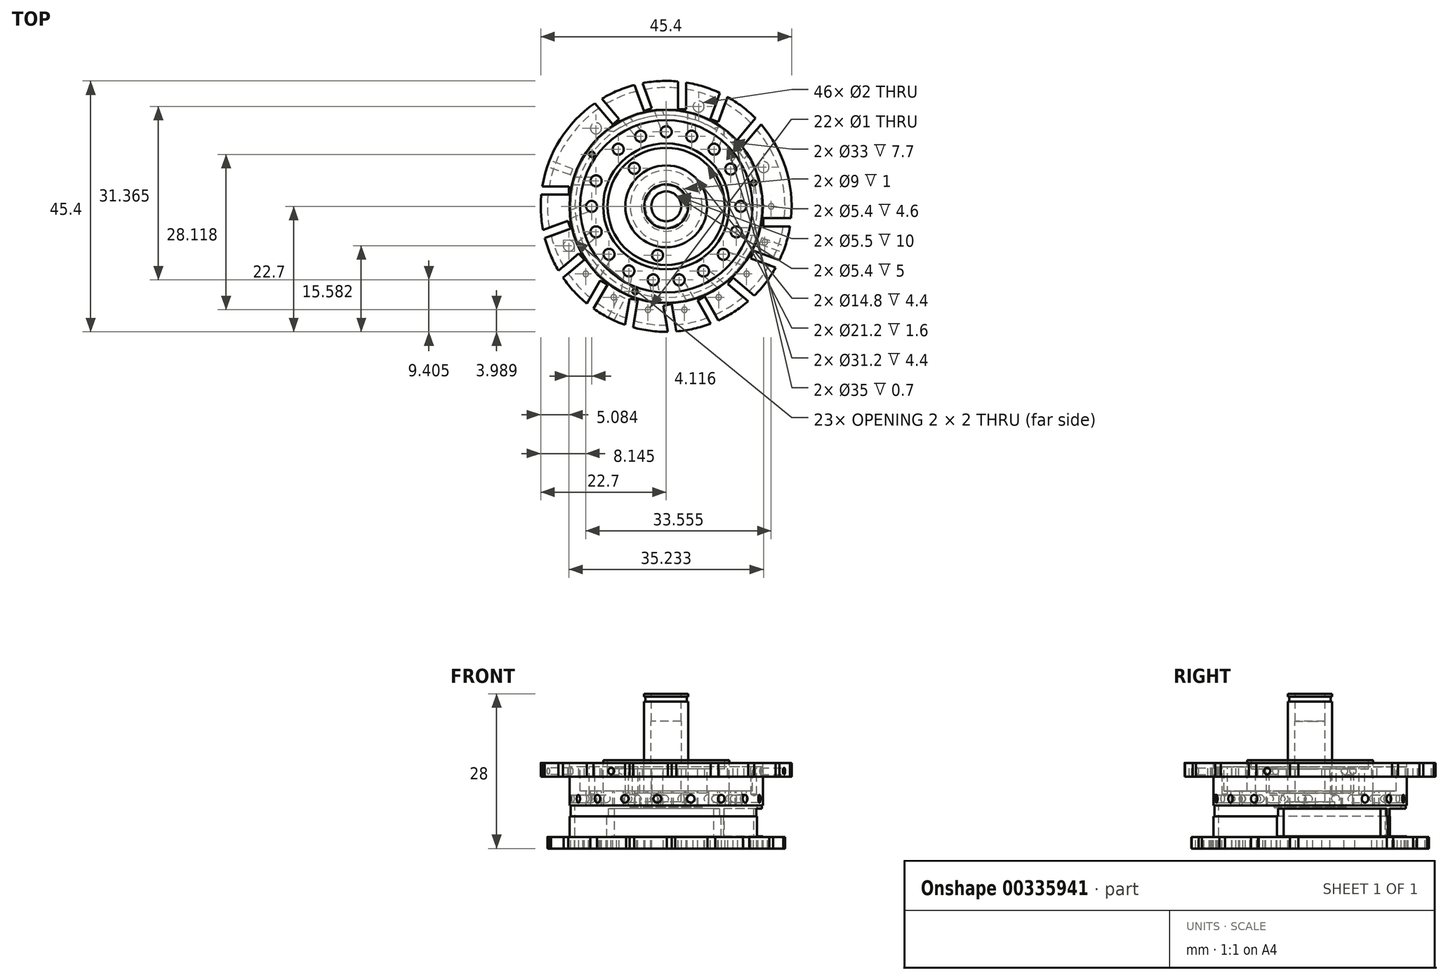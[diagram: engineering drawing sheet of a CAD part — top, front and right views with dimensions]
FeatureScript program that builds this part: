
annotation { "Feature Type Name" : "Feature", "Feature Type Description" : "" }
export const myFeature = defineFeature(function(context is Context, id is Id, definition is map)
    precondition{}
    {
        {
            var Q0;
            Q0=qCreatedBy(makeId("Front.planeOp"),FACE);
            var sketch = newSketch(context, id + "F0", { "sketchPlane" : qUnion([Q0])});
            skLineSegment(sketch, "E0", {"start": v(-16.5, 0) * mm, "end": v(-16.5, 7.7) * mm});
            skLineSegment(sketch, "E1", {"start": v(-16.5, 7.7) * mm, "end": v(-6.5, 7.7) * mm});
            skLineSegment(sketch, "E2", {"start": v(-6.5, 7.7) * mm, "end": v(-6.5, 7.4) * mm});
            skLineSegment(sketch, "E3", {"start": v(-6.5, 7.4) * mm, "end": v(-4.5, 7.4) * mm});
            skLineSegment(sketch, "E4", {"start": v(-4.5, 7.4) * mm, "end": v(-4.5, 8.4) * mm});
            skLineSegment(sketch, "E5", {"start": v(-4.5, 8.4) * mm, "end": v(-2.7, 8.4) * mm});
            skLineSegment(sketch, "E6", {"start": v(-2.7, 8.4) * mm, "end": v(-2.7, 13) * mm});
            skLineSegment(sketch, "E7", {"start": v(-2.7, 13) * mm, "end": v(-2.75, 13) * mm});
            skLineSegment(sketch, "E8", {"start": v(-2.75, 13) * mm, "end": v(-2.75, 23) * mm});
            skLineSegment(sketch, "E9", {"start": v(-2.75, 23) * mm, "end": v(-2.7, 23) * mm});
            skLineSegment(sketch, "E10", {"start": v(-2.7, 23) * mm, "end": v(-2.7, 28) * mm});
            skLineSegment(sketch, "E11", {"start": v(-2.7, 28) * mm, "end": v(-4, 28) * mm});
            skLineSegment(sketch, "E12", {"start": v(-4, 28) * mm, "end": v(-4, 27.5) * mm});
            skLineSegment(sketch, "E13", {"start": v(-4, 27.5) * mm, "end": v(-3.75, 27.5) * mm});
            skLineSegment(sketch, "E14", {"start": v(-3.75, 27.5) * mm, "end": v(-3.75, 26.6) * mm});
            skLineSegment(sketch, "E15", {"start": v(-3.75, 26.6) * mm, "end": v(-4, 26.6) * mm});
            skLineSegment(sketch, "E16", {"start": v(-4, 26.6) * mm, "end": v(-4, 10) * mm});
            skLineSegment(sketch, "E17", {"start": v(-4, 10) * mm, "end": v(-7.4, 10) * mm});
            skLineSegment(sketch, "E18", {"start": v(-7.4, 10) * mm, "end": v(-7.4, 14.4) * mm});
            skLineSegment(sketch, "E19", {"start": v(-7.4, 14.4) * mm, "end": v(-10.6, 14.4) * mm});
            skLineSegment(sketch, "E20", {"start": v(-10.6, 14.4) * mm, "end": v(-10.6, 16) * mm});
            skLineSegment(sketch, "E21", {"start": v(-10.6, 16) * mm, "end": v(-11.4, 16) * mm});
            skLineSegment(sketch, "E22", {"start": v(-11.4, 16) * mm, "end": v(-11.4, 10.4) * mm});
            skLineSegment(sketch, "E23", {"start": v(-22.7, 15.5) * mm, "end": v(-22.7, 13) * mm});
            skLineSegment(sketch, "E24", {"start": v(-22.7, 13) * mm, "end": v(-17.5, 13) * mm});
            skLineSegment(sketch, "E25", {"start": v(-17.5, 13) * mm, "end": v(-17.5, 7.8) * mm});
            skLineSegment(sketch, "E26", {"start": v(-17.5, 7.8) * mm, "end": v(-17.3, 7.8) * mm});
            skLineSegment(sketch, "E27", {"start": v(-17.3, 7.8) * mm, "end": v(-17.3, 5.8) * mm});
            skLineSegment(sketch, "E28", {"start": v(-17.3, 5.8) * mm, "end": v(-17.5, 5.8) * mm});
            skLineSegment(sketch, "E29", {"start": v(-17.5, 5.8) * mm, "end": v(-17.5, 2.1) * mm});
            skLineSegment(sketch, "E30", {"start": v(-17.5, 2.1) * mm, "end": v(-21.5, 2.1) * mm});
            skLineSegment(sketch, "E31", {"start": v(-21.5, 2.1) * mm, "end": v(-21.5, 0) * mm});
            skLineSegment(sketch, "E32", {"start": v(-21.5, 0) * mm, "end": v(-16.5, 0) * mm});
            skLineSegment(sketch, "E33", {"start": v(0, 28) * mm, "end": v(0, 0) * mm});
            skLineSegment(sketch, "E34", {"start": v(-11.4, 10.4) * mm, "end": v(-15.6, 10.4) * mm});
            skLineSegment(sketch, "E35", {"start": v(-15.6, 10.4) * mm, "end": v(-15.6, 14.8) * mm});
            skLineSegment(sketch, "E36", {"start": v(-15.6, 14.8) * mm, "end": v(-17.5, 14.8) * mm});
            skLineSegment(sketch, "E37", {"start": v(-17.5, 14.8) * mm, "end": v(-17.5, 15.5) * mm});
            skLineSegment(sketch, "E38", {"start": v(-17.5, 15.5) * mm, "end": v(-22.7, 15.5) * mm});
            skSolve(sketch);
        }
        {
            var Q0;
            Q0 = qSketchRegion(id + "F0", true);
            var Q1;
            Q1=sQuery(id+"F0.wireOp",EDGE,"E33");
            revolve(context, id + "F1", {"entities" : qUnion([Q0]), "axis" : qUnion([Q1]), "revolveType" : RevolveType.FULL});
        }
        {
            var Q0;
            Q0=makeQuery(id+"F1.opRevolve","SWEPT_FACE",FACE,{"disambiguationData":[OSD([sQuery(id+"F0.wireOp",EDGE,"E38")])]});
            var sketch = newSketch(context, id + "F2", { "sketchPlane" : qUnion([Q0])});
            skCircle(sketch, "E39.0", {"center": v(0, 0) * mm, "radius": 22.7 * mm, "construction": true});
            skCircle(sketch, "E40", {"center": v(0, 0) * mm, "radius": 13.5 * mm, "construction": true});
            skCircle(sketch, "E41", {"center": v(13.5, 0) * mm, "radius": 1 * mm});
            skLineSegment(sketch, "E42", {"start": v(0, 0) * mm, "end": v(-8.68, 10.34) * mm, "construction": true});
            skCircle(sketch, "E43", {"center": v(-8.68, 10.34) * mm, "radius": 1 * mm});
            skLineSegment(sketch, "E44", {"start": v(0, 0) * mm, "end": v(21.33, -7.76) * mm, "construction": true});
            skCircle(sketch, "E45", {"center": v(12.69, -4.62) * mm, "radius": 1 * mm});
            skLineSegment(sketch, "E46", {"start": v(12.69, -4.62) * mm, "end": v(22.23, -4.62) * mm, "construction": true});
            skLineSegment(sketch, "E47", {"start": v(22.6, -3.62) * mm, "end": v(17.6, -3.62) * mm});
            skLineSegment(sketch, "E48", {"start": v(17.6, -3.62) * mm, "end": v(17.6, -2.12) * mm});
            skLineSegment(sketch, "E49", {"start": v(17.6, -2.12) * mm, "end": v(22.6, -2.12) * mm});
            skLineSegment(sketch, "E50.1.0", {"start": v(15.81, -8) * mm, "end": v(20.51, -9.72) * mm});
            skLineSegment(sketch, "E50.1.1", {"start": v(20, -11.13) * mm, "end": v(15.3, -9.42) * mm});
            skLineSegment(sketch, "E50.1.2", {"start": v(15.3, -9.42) * mm, "end": v(15.81, -8) * mm});
            skCircle(sketch, "E50.1.3", {"center": v(10.34, -8.68) * mm, "radius": 1 * mm});
            skLineSegment(sketch, "E50.2.0", {"start": v(12.12, -12.93) * mm, "end": v(15.95, -16.15) * mm});
            skLineSegment(sketch, "E50.2.1", {"start": v(14.99, -17.3) * mm, "end": v(11.16, -14.08) * mm});
            skLineSegment(sketch, "E50.2.2", {"start": v(11.16, -14.08) * mm, "end": v(12.12, -12.93) * mm});
            skCircle(sketch, "E50.2.3", {"center": v(6.75, -11.7) * mm, "radius": 1 * mm});
            skLineSegment(sketch, "E50.3.0", {"start": v(6.97, -16.3) * mm, "end": v(9.47, -20.63) * mm});
            skLineSegment(sketch, "E50.3.1", {"start": v(8.17, -21.38) * mm, "end": v(5.67, -17.05) * mm});
            skLineSegment(sketch, "E50.3.2", {"start": v(5.67, -17.05) * mm, "end": v(6.97, -16.3) * mm});
            skCircle(sketch, "E50.3.3", {"center": v(2.34, -13.3) * mm, "radius": 1 * mm});
            skLineSegment(sketch, "E50.4.0", {"start": v(0.97, -17.7) * mm, "end": v(1.84, -22.63) * mm});
            skLineSegment(sketch, "E50.4.1", {"start": v(0.36, -22.89) * mm, "end": v(-0.5, -17.96) * mm});
            skLineSegment(sketch, "E50.4.2", {"start": v(-0.5, -17.96) * mm, "end": v(0.97, -17.7) * mm});
            skCircle(sketch, "E50.4.3", {"center": v(-2.34, -13.3) * mm, "radius": 1 * mm});
            skLineSegment(sketch, "E50.5.0", {"start": v(-5.14, -16.96) * mm, "end": v(-6, -21.9) * mm});
            skLineSegment(sketch, "E50.5.1", {"start": v(-7.49, -21.63) * mm, "end": v(-6.62, -16.7) * mm});
            skLineSegment(sketch, "E50.5.2", {"start": v(-6.62, -16.7) * mm, "end": v(-5.14, -16.96) * mm});
            skCircle(sketch, "E50.5.3", {"center": v(-6.75, -11.7) * mm, "radius": 1 * mm});
            skLineSegment(sketch, "E50.6.0", {"start": v(-10.63, -14.18) * mm, "end": v(-13.13, -18.51) * mm});
            skLineSegment(sketch, "E50.6.1", {"start": v(-14.43, -17.76) * mm, "end": v(-11.93, -13.43) * mm});
            skLineSegment(sketch, "E50.6.2", {"start": v(-11.93, -13.43) * mm, "end": v(-10.63, -14.18) * mm});
            skCircle(sketch, "E50.6.3", {"center": v(-10.34, -8.68) * mm, "radius": 1 * mm});
            skLineSegment(sketch, "E50.7.0", {"start": v(-14.84, -9.7) * mm, "end": v(-18.67, -12.9) * mm});
            skLineSegment(sketch, "E50.7.1", {"start": v(-19.64, -11.76) * mm, "end": v(-15.8, -8.54) * mm});
            skLineSegment(sketch, "E50.7.2", {"start": v(-15.8, -8.54) * mm, "end": v(-14.84, -9.7) * mm});
            skCircle(sketch, "E50.7.3", {"center": v(-12.69, -4.62) * mm, "radius": 1 * mm});
            skLineSegment(sketch, "E50.8.0", {"start": v(-17.26, -4.03) * mm, "end": v(-21.96, -5.74) * mm});
            skLineSegment(sketch, "E50.8.1", {"start": v(-22.48, -4.33) * mm, "end": v(-17.78, -2.62) * mm});
            skLineSegment(sketch, "E50.8.2", {"start": v(-17.78, -2.62) * mm, "end": v(-17.26, -4.03) * mm});
            skCircle(sketch, "E50.8.3", {"center": v(-13.5, 0) * mm, "radius": 1 * mm});
            skLineSegment(sketch, "E50.9.0", {"start": v(-17.6, 2.12) * mm, "end": v(-22.6, 2.12) * mm});
            skLineSegment(sketch, "E50.9.1", {"start": v(-22.6, 3.62) * mm, "end": v(-17.6, 3.62) * mm});
            skLineSegment(sketch, "E50.9.2", {"start": v(-17.6, 3.62) * mm, "end": v(-17.6, 2.12) * mm});
            skCircle(sketch, "E50.9.3", {"center": v(-12.69, 4.62) * mm, "radius": 1 * mm});
            skLineSegment(sketch, "E50.anchor1", {"start": v(0, 0) * mm, "end": v(17.6, -2.12) * mm, "construction": true});
            skLineSegment(sketch, "E50.anchor2", {"start": v(0, 0) * mm, "end": v(-17.6, 2.12) * mm, "construction": true});
            skLineSegment(sketch, "E51", {"start": v(0, 0) * mm, "end": v(-7.76, 21.33) * mm, "construction": true});
            skCircle(sketch, "E52", {"center": v(-4.62, 12.69) * mm, "radius": 1 * mm});
            skLineSegment(sketch, "E53", {"start": v(-4.62, 12.69) * mm, "end": v(-10.75, 20) * mm, "construction": true});
            skLineSegment(sketch, "E54", {"start": v(-11.76, 19.64) * mm, "end": v(-8.54, 15.8) * mm});
            skLineSegment(sketch, "E55", {"start": v(-8.54, 15.8) * mm, "end": v(-9.7, 14.84) * mm});
            skLineSegment(sketch, "E56", {"start": v(-9.7, 14.84) * mm, "end": v(-12.9, 18.67) * mm});
            skCircle(sketch, "E57.1.0", {"center": v(0, 13.5) * mm, "radius": 1 * mm});
            skLineSegment(sketch, "E57.1.1", {"start": v(-4.33, 22.48) * mm, "end": v(-2.62, 17.78) * mm});
            skLineSegment(sketch, "E57.1.2", {"start": v(-2.62, 17.78) * mm, "end": v(-4.03, 17.26) * mm});
            skLineSegment(sketch, "E57.1.3", {"start": v(-4.03, 17.26) * mm, "end": v(-5.74, 21.96) * mm});
            skCircle(sketch, "E57.2.0", {"center": v(4.62, 12.69) * mm, "radius": 1 * mm});
            skLineSegment(sketch, "E57.2.1", {"start": v(3.62, 22.6) * mm, "end": v(3.62, 17.6) * mm});
            skLineSegment(sketch, "E57.2.2", {"start": v(3.62, 17.6) * mm, "end": v(2.12, 17.6) * mm});
            skLineSegment(sketch, "E57.2.3", {"start": v(2.12, 17.6) * mm, "end": v(2.12, 22.6) * mm});
            skCircle(sketch, "E57.3.0", {"center": v(8.68, 10.34) * mm, "radius": 1 * mm});
            skLineSegment(sketch, "E57.3.1", {"start": v(11.13, 20) * mm, "end": v(9.42, 15.3) * mm});
            skLineSegment(sketch, "E57.3.2", {"start": v(9.42, 15.3) * mm, "end": v(8, 15.81) * mm});
            skLineSegment(sketch, "E57.3.3", {"start": v(8, 15.81) * mm, "end": v(9.72, 20.51) * mm});
            skCircle(sketch, "E57.4.0", {"center": v(11.7, 6.75) * mm, "radius": 1 * mm});
            skLineSegment(sketch, "E57.4.1", {"start": v(17.3, 14.99) * mm, "end": v(14.08, 11.16) * mm});
            skLineSegment(sketch, "E57.4.2", {"start": v(14.08, 11.16) * mm, "end": v(12.93, 12.12) * mm});
            skLineSegment(sketch, "E57.4.3", {"start": v(12.93, 12.12) * mm, "end": v(16.15, 15.95) * mm});
            skLineSegment(sketch, "E57.anchor1", {"start": v(0, 0) * mm, "end": v(-4.62, 12.69) * mm, "construction": true});
            skLineSegment(sketch, "E57.anchor2", {"start": v(0, 0) * mm, "end": v(11.7, 6.75) * mm, "construction": true});
            skLineSegment(sketch, "E58", {"start": v(22.6, -2.12) * mm, "end": v(22.6, -3.62) * mm});
            skPoint(sketch, "E59.orphan", {"position": v(22.4, -3.62) * mm});
            skLineSegment(sketch, "E60", {"start": v(20.51, -9.72) * mm, "end": v(20, -11.13) * mm});
            skPoint(sketch, "E61.orphan", {"position": v(19.82, -11.06) * mm});
            skLineSegment(sketch, "E62", {"start": v(15.95, -16.15) * mm, "end": v(14.99, -17.3) * mm});
            skPoint(sketch, "E63.orphan", {"position": v(14.84, -17.18) * mm});
            skLineSegment(sketch, "E64", {"start": v(9.47, -20.63) * mm, "end": v(8.17, -21.38) * mm});
            skPoint(sketch, "E65.orphan", {"position": v(8.07, -21.22) * mm});
            skLineSegment(sketch, "E66", {"start": v(1.84, -22.63) * mm, "end": v(0.36, -22.89) * mm});
            skPoint(sketch, "E67.orphan", {"position": v(0.33, -22.7) * mm});
            skLineSegment(sketch, "E68", {"start": v(-6, -21.9) * mm, "end": v(-7.49, -21.63) * mm});
            skPoint(sketch, "E69.orphan", {"position": v(-7.45, -21.44) * mm});
            skLineSegment(sketch, "E70", {"start": v(-13.13, -18.51) * mm, "end": v(-14.43, -17.76) * mm});
            skPoint(sketch, "E71.orphan", {"position": v(-14.34, -17.6) * mm});
            skLineSegment(sketch, "E72", {"start": v(-18.67, -12.9) * mm, "end": v(-19.64, -11.76) * mm});
            skPoint(sketch, "E73.orphan", {"position": v(-19.5, -11.63) * mm});
            skLineSegment(sketch, "E74", {"start": v(-21.96, -5.74) * mm, "end": v(-22.48, -4.33) * mm});
            skPoint(sketch, "E75.orphan", {"position": v(-22.3, -4.27) * mm});
            skLineSegment(sketch, "E76", {"start": v(-22.6, 2.12) * mm, "end": v(-22.6, 3.62) * mm});
            skPoint(sketch, "E77.orphan", {"position": v(-22.4, 3.62) * mm});
            skLineSegment(sketch, "E78", {"start": v(-12.9, 18.67) * mm, "end": v(-11.76, 19.64) * mm});
            skPoint(sketch, "E79.orphan", {"position": v(-11.63, 19.5) * mm});
            skLineSegment(sketch, "E80", {"start": v(-5.74, 21.96) * mm, "end": v(-4.33, 22.48) * mm});
            skPoint(sketch, "E81.orphan", {"position": v(-4.27, 22.3) * mm});
            skLineSegment(sketch, "E82", {"start": v(2.12, 22.6) * mm, "end": v(3.62, 22.6) * mm});
            skPoint(sketch, "E83.orphan", {"position": v(3.62, 22.4) * mm});
            skLineSegment(sketch, "E84", {"start": v(9.72, 20.51) * mm, "end": v(11.13, 20) * mm});
            skPoint(sketch, "E85.orphan", {"position": v(11.06, 19.82) * mm});
            skLineSegment(sketch, "E86", {"start": v(16.15, 15.95) * mm, "end": v(17.3, 14.99) * mm});
            skPoint(sketch, "E87.orphan", {"position": v(17.18, 14.84) * mm});
            skCircle(sketch, "E88", {"center": v(0, 0) * mm, "radius": 9 * mm, "construction": true});
            skCircle(sketch, "E89", {"center": v(-5.79, 6.9) * mm, "radius": 1 * mm});
            skCircle(sketch, "E90", {"center": v(-1.56, -8.86) * mm, "radius": 1 * mm});
            skLineSegment(sketch, "E91", {"start": v(0, 0) * mm, "end": v(-2.34, -13.3) * mm, "construction": true});
            skSolve(sketch);
        }
        {
            var Q0;
            Q0 = qSketchRegion(id + "F2", true);
            extrude(context, id + "F3", {"entities" : qUnion([Q0]), "operationType" : NewBodyOperationType.REMOVE, "endBound" : BoundingType.THROUGH_ALL, "oppositeDirection" : true, "depth" : 25 * mm});
        }
        {
            var Q0;
            Q0=makeQuery(id+"F1.opRevolve","SWEPT_FACE",FACE,{"disambiguationData":[OSD([sQuery(id+"F0.wireOp",EDGE,"E36")])]});
            var sketch = newSketch(context, id + "F4", { "sketchPlane" : qUnion([Q0])});
            skCircle(sketch, "E92", {"center": v(0, 0) * mm, "radius": 16.4 * mm, "construction": true});
            skLineSegment(sketch, "E93", {"start": v(0, 0) * mm, "end": v(15.84, 4.24) * mm, "construction": true});
            skLineSegment(sketch, "E94", {"start": v(0, 0) * mm, "end": v(-5.6, -15.41) * mm, "construction": true});
            skLineSegment(sketch, "E95", {"start": v(0, 0) * mm, "end": v(-13.43, 9.4) * mm, "construction": true});
            skSolve(sketch);
        }
        {
            var Q0;
            Q0=sQuery(id+"F4.wireOp",VERTEX,"E95.end");
            var Q1;
            Q1=sQuery(id+"F4.wireOp",VERTEX,"E94.end");
            var Q2;
            Q2=sQuery(id+"F4.wireOp",VERTEX,"E93.end");
            var Q3;
            Q3=makeQuery(id+"F1.opRevolve","SWEPT_BODY",BODY,{"disambiguationData":[OSD([sQuery(id+"F0.wireOp",EDGE,"E0"),sQuery(id+"F0.wireOp",EDGE,"E1"),sQuery(id+"F0.wireOp",EDGE,"E2"),sQuery(id+"F0.wireOp",EDGE,"E3"),sQuery(id+"F0.wireOp",EDGE,"E4"),sQuery(id+"F0.wireOp",EDGE,"E5"),sQuery(id+"F0.wireOp",EDGE,"E6"),sQuery(id+"F0.wireOp",EDGE,"E7"),sQuery(id+"F0.wireOp",EDGE,"E8"),sQuery(id+"F0.wireOp",EDGE,"E9"),sQuery(id+"F0.wireOp",EDGE,"E10"),sQuery(id+"F0.wireOp",EDGE,"E11"),sQuery(id+"F0.wireOp",EDGE,"E12"),sQuery(id+"F0.wireOp",EDGE,"E13"),sQuery(id+"F0.wireOp",EDGE,"E14"),sQuery(id+"F0.wireOp",EDGE,"E15"),sQuery(id+"F0.wireOp",EDGE,"E16"),sQuery(id+"F0.wireOp",EDGE,"E17"),sQuery(id+"F0.wireOp",EDGE,"E18"),sQuery(id+"F0.wireOp",EDGE,"E19"),sQuery(id+"F0.wireOp",EDGE,"E20"),sQuery(id+"F0.wireOp",EDGE,"E21"),sQuery(id+"F0.wireOp",EDGE,"E22"),sQuery(id+"F0.wireOp",EDGE,"E23"),sQuery(id+"F0.wireOp",EDGE,"E24"),sQuery(id+"F0.wireOp",EDGE,"E25"),sQuery(id+"F0.wireOp",EDGE,"E26"),sQuery(id+"F0.wireOp",EDGE,"E27"),sQuery(id+"F0.wireOp",EDGE,"E28"),sQuery(id+"F0.wireOp",EDGE,"E29"),sQuery(id+"F0.wireOp",EDGE,"E30"),sQuery(id+"F0.wireOp",EDGE,"E31"),sQuery(id+"F0.wireOp",EDGE,"E32"),sQuery(id+"F0.wireOp",EDGE,"E34"),sQuery(id+"F0.wireOp",EDGE,"E35"),sQuery(id+"F0.wireOp",EDGE,"E36"),sQuery(id+"F0.wireOp",EDGE,"E37"),sQuery(id+"F0.wireOp",EDGE,"E38")])]});
            hole(context, id + "F5", {"style" : HoleStyle.SIMPLE, "endStyle" : HoleEndStyle.BLIND, "holeDiameter" : 1 * mm, "holeDepth" : 5 * mm, "tappedDepth" : 12 * mm, "tapClearance" : 3, "locations" : qUnion([Q0, Q1, Q2]), "scope" : qUnion([Q3])});
        }
        {
            var Q0;
            Q0=makeQuery(id+"F1.opRevolve","SWEPT_FACE",FACE,{"disambiguationData":[OSD([sQuery(id+"F0.wireOp",EDGE,"E21")])]});
            cPlane(context, id + "F6", {"entities" : qUnion([Q0]), "cplaneType" : CPlaneType.OFFSET, "offset" : 2 * mm, "oppositeDirection" : true, "width" : 150 * mm, "height" : 150 * mm});
        }
        {
            var Q0;
            Q0=qCreatedBy(id+"F6.planeOp",FACE);
            var sketch = newSketch(context, id + "F7", { "sketchPlane" : qUnion([Q0])});
            skCircle(sketch, "E96.0", {"center": v(0, 0) * mm, "radius": 22.7 * mm, "construction": true});
            skLineSegment(sketch, "E97", {"start": v(0, 0) * mm, "end": v(21.33, -7.76) * mm, "construction": true});
            skLineSegment(sketch, "E98", {"start": v(0, 0) * mm, "end": v(-9.95, -20.4) * mm, "construction": true});
            skLineSegment(sketch, "E99", {"start": v(0, 0) * mm, "end": v(-21.33, 7.76) * mm, "construction": true});
            skLineSegment(sketch, "E100.bottom", {"start": v(-21.13, 8.33) * mm, "end": v(-16.9, 6.79) * mm});
            skLineSegment(sketch, "E100.top", {"start": v(-21.54, 7.2) * mm, "end": v(-17.3, 5.66) * mm});
            skLineSegment(sketch, "E100.left", {"start": v(-21.13, 8.33) * mm, "end": v(-21.54, 7.2) * mm});
            skLineSegment(sketch, "E100.right", {"start": v(-16.9, 6.79) * mm, "end": v(-17.3, 5.66) * mm});
            skPoint(sketch, "E101", {"position": v(-21.33, 7.76) * mm});
            skLineSegment(sketch, "E102", {"start": v(-21.33, 7.76) * mm, "end": v(-17.1, 6.22) * mm});
            skLineSegment(sketch, "E103.bottom", {"start": v(17.3, -5.66) * mm, "end": v(21.54, -7.2) * mm});
            skLineSegment(sketch, "E103.top", {"start": v(16.9, -6.79) * mm, "end": v(21.13, -8.33) * mm});
            skLineSegment(sketch, "E103.left", {"start": v(17.3, -5.66) * mm, "end": v(16.9, -6.79) * mm});
            skLineSegment(sketch, "E103.right", {"start": v(21.54, -7.2) * mm, "end": v(21.13, -8.33) * mm});
            skLineSegment(sketch, "E104.bottom", {"start": v(-10.5, -20.14) * mm, "end": v(-9.41, -20.67) * mm});
            skLineSegment(sketch, "E104.top", {"start": v(-8.52, -16.1) * mm, "end": v(-7.44, -16.62) * mm});
            skLineSegment(sketch, "E104.left", {"start": v(-10.5, -20.14) * mm, "end": v(-8.52, -16.1) * mm});
            skLineSegment(sketch, "E104.right", {"start": v(-9.41, -20.67) * mm, "end": v(-7.44, -16.62) * mm});
            skPoint(sketch, "E105", {"position": v(-9.95, -20.4) * mm});
            skPoint(sketch, "E106", {"position": v(21.33, -7.76) * mm});
            skLineSegment(sketch, "E107", {"start": v(-9.95, -20.4) * mm, "end": v(-7.98, -16.36) * mm});
            skLineSegment(sketch, "E108", {"start": v(17.1, -6.22) * mm, "end": v(21.33, -7.76) * mm});
            skSolve(sketch);
        }
        {
            var Q0;
            Q0=makeQuery(id+"F7.imprint","IMPRINT",FACE,{"disambiguationData":[TD([[makeQuery(id+"F7.imprint","IMPRINT",EDGE,{"derivedFrom":sQuery(id+"F7.wireOp",EDGE,"E100.bottom")}),-1.0]])]});
            var Q1;
            Q1=sQuery(id+"F7.wireOp",EDGE,"E99");
            revolve(context, id + "F8", {"operationType" : NewBodyOperationType.REMOVE, "entities" : qUnion([Q0]), "axis" : qUnion([Q1]), "revolveType" : RevolveType.FULL, "oppositeDirection" : true});
        }
        {
            var Q0;
            {var subQ0=sQuery(id+"F7.wireOp",EDGE,"E103.bottom");Q0=makeQuery(id+"F7.imprint","IMPRINT",FACE,{"disambiguationData":[TD([[makeQuery(id+"F7.imprint","IMPRINT",EDGE,{"derivedFrom":subQ0}),-1.0]])]});}
            var Q1;
            Q1=sQuery(id+"F7.wireOp",EDGE,"E108");
            revolve(context, id + "F9", {"operationType" : NewBodyOperationType.REMOVE, "entities" : qUnion([Q0]), "axis" : qUnion([Q1]), "revolveType" : RevolveType.FULL, "oppositeDirection" : true});
        }
        {
            var Q0;
            {var subQ0=sQuery(id+"F7.wireOp",EDGE,"E104.right");Q0=makeQuery(id+"F7.imprint","IMPRINT",FACE,{"disambiguationData":[TD([[makeQuery(id+"F7.imprint","IMPRINT",EDGE,{"derivedFrom":subQ0}),1.0]])]});}
            var Q1;
            Q1=sQuery(id+"F7.wireOp",EDGE,"E107");
            revolve(context, id + "F10", {"operationType" : NewBodyOperationType.REMOVE, "entities" : qUnion([Q0]), "axis" : qUnion([Q1]), "revolveType" : RevolveType.FULL, "oppositeDirection" : true});
        }
        {
            var Q0;
            Q0=makeQuery(id+"F1.opRevolve","SWEPT_FACE",FACE,{"disambiguationData":[OSD([sQuery(id+"F0.wireOp",EDGE,"E21")])]});
            cPlane(context, id + "F11", {"entities" : qUnion([Q0]), "cplaneType" : CPlaneType.OFFSET, "offset" : 7 * mm, "oppositeDirection" : true, "width" : 150 * mm, "height" : 150 * mm});
        }
        {
            var Q0;
            Q0=qCreatedBy(id+"F11.planeOp",FACE);
            var sketch = newSketch(context, id + "F12", { "sketchPlane" : qUnion([Q0])});
            skCircle(sketch, "E109", {"center": v(0, 0) * mm, "radius": 13.5 * mm, "construction": true});
            skLineSegment(sketch, "E110", {"start": v(0, 0) * mm, "end": v(12.69, -4.62) * mm, "construction": true});
            skCircle(sketch, "E111", {"center": v(0, 0) * mm, "radius": 21.5 * mm, "construction": true});
            skLineSegment(sketch, "E112", {"start": v(12.69, -4.62) * mm, "end": v(21, -4.62) * mm});
            skLineSegment(sketch, "E113.bottom", {"start": v(12.69, -3.92) * mm, "end": v(21, -3.92) * mm});
            skLineSegment(sketch, "E113.top", {"start": v(12.69, -5.32) * mm, "end": v(21, -5.32) * mm});
            skLineSegment(sketch, "E113.left", {"start": v(12.69, -3.92) * mm, "end": v(12.69, -5.32) * mm});
            skLineSegment(sketch, "E113.right", {"start": v(21, -3.92) * mm, "end": v(21, -5.32) * mm});
            skPoint(sketch, "E114", {"position": v(12.69, -4.62) * mm});
            skPoint(sketch, "E115", {"position": v(21, -4.62) * mm});
            skLineSegment(sketch, "E116", {"start": v(0, 0) * mm, "end": v(-8.68, 10.34) * mm, "construction": true});
            skLineSegment(sketch, "E117", {"start": v(0, 0) * mm, "end": v(-4.62, 12.69) * mm, "construction": true});
            skLineSegment(sketch, "E118.bottom", {"start": v(-9.42, 19.5) * mm, "end": v(-4.08, 13.14) * mm});
            skLineSegment(sketch, "E118.top", {"start": v(-10.5, 18.6) * mm, "end": v(-5.15, 12.24) * mm});
            skLineSegment(sketch, "E118.left", {"start": v(-9.42, 19.5) * mm, "end": v(-10.5, 18.6) * mm});
            skLineSegment(sketch, "E118.right", {"start": v(-4.08, 13.14) * mm, "end": v(-5.15, 12.24) * mm});
            skPoint(sketch, "E119", {"position": v(-9.96, 19.05) * mm});
            skPoint(sketch, "E120", {"position": v(-4.62, 12.69) * mm});
            skLineSegment(sketch, "E121", {"start": v(-9.96, 19.05) * mm, "end": v(-4.62, 12.69) * mm});
            skSolve(sketch);
        }
        {
            var Q0;
            {var subQ0=sQuery(id+"F12.wireOp",EDGE,"E112");Q0=makeQuery(id+"F12.imprint","IMPRINT",FACE,{"disambiguationData":[TD([[makeQuery(id+"F12.imprint","IMPRINT",EDGE,{"derivedFrom":subQ0}),1.0]])]});}
            var Q1;
            Q1=sQuery(id+"F12.wireOp",EDGE,"E112");
            revolve(context, id + "F13", {"entities" : qUnion([Q0]), "axis" : qUnion([Q1]), "revolveType" : RevolveType.FULL});
        }
        {
            var Q0;
            Q0=makeQuery(id+"F13.opRevolve","SWEPT_BODY",BODY,{"disambiguationData":[OSD([sQuery(id+"F12.wireOp",EDGE,"E112"),sQuery(id+"F12.wireOp",EDGE,"E113.bottom"),sQuery(id+"F12.wireOp",EDGE,"E113.left"),sQuery(id+"F12.wireOp",EDGE,"E113.right")])]});
            var Q1;
            Q1=sQuery(id+"F0.wireOp",EDGE,"E33");
            circularPattern(context, id + "F14", {"entities" : qUnion([Q0]), "axis" : qUnion([Q1]), "angle" : 180 * degree, "instanceCount" : 10, "equalSpace" : true});
        }
        {
            var Q0;
            Q0=makeQuery(id+"F13.opRevolve","SWEPT_BODY",BODY,{"disambiguationData":[OSD([sQuery(id+"F12.wireOp",EDGE,"E112"),sQuery(id+"F12.wireOp",EDGE,"E113.bottom"),sQuery(id+"F12.wireOp",EDGE,"E113.left"),sQuery(id+"F12.wireOp",EDGE,"E113.right")])]});
            var Q1;
            Q1=makeQuery(id+"F14.opPattern","COPY",BODY,{"derivedFrom":makeQuery(id+"F13.opRevolve","SWEPT_BODY",BODY,{"disambiguationData":[OSD([sQuery(id+"F12.wireOp",EDGE,"E112"),sQuery(id+"F12.wireOp",EDGE,"E113.bottom"),sQuery(id+"F12.wireOp",EDGE,"E113.left"),sQuery(id+"F12.wireOp",EDGE,"E113.right")])]}),"instanceName":"2"});
            var Q2;
            Q2=makeQuery(id+"F14.opPattern","COPY",BODY,{"derivedFrom":makeQuery(id+"F13.opRevolve","SWEPT_BODY",BODY,{"disambiguationData":[OSD([sQuery(id+"F12.wireOp",EDGE,"E112"),sQuery(id+"F12.wireOp",EDGE,"E113.bottom"),sQuery(id+"F12.wireOp",EDGE,"E113.left"),sQuery(id+"F12.wireOp",EDGE,"E113.right")])]}),"instanceName":"3"});
            var Q3;
            Q3=makeQuery(id+"F14.opPattern","COPY",BODY,{"derivedFrom":makeQuery(id+"F13.opRevolve","SWEPT_BODY",BODY,{"disambiguationData":[OSD([sQuery(id+"F12.wireOp",EDGE,"E112"),sQuery(id+"F12.wireOp",EDGE,"E113.bottom"),sQuery(id+"F12.wireOp",EDGE,"E113.left"),sQuery(id+"F12.wireOp",EDGE,"E113.right")])]}),"instanceName":"1"});
            var Q4;
            Q4=makeQuery(id+"F14.opPattern","COPY",BODY,{"derivedFrom":makeQuery(id+"F13.opRevolve","SWEPT_BODY",BODY,{"disambiguationData":[OSD([sQuery(id+"F12.wireOp",EDGE,"E112"),sQuery(id+"F12.wireOp",EDGE,"E113.bottom"),sQuery(id+"F12.wireOp",EDGE,"E113.left"),sQuery(id+"F12.wireOp",EDGE,"E113.right")])]}),"instanceName":"4"});
            var Q5;
            Q5=makeQuery(id+"F14.opPattern","COPY",BODY,{"derivedFrom":makeQuery(id+"F13.opRevolve","SWEPT_BODY",BODY,{"disambiguationData":[OSD([sQuery(id+"F12.wireOp",EDGE,"E112"),sQuery(id+"F12.wireOp",EDGE,"E113.bottom"),sQuery(id+"F12.wireOp",EDGE,"E113.left"),sQuery(id+"F12.wireOp",EDGE,"E113.right")])]}),"instanceName":"5"});
            var Q6;
            Q6=makeQuery(id+"F14.opPattern","COPY",BODY,{"derivedFrom":makeQuery(id+"F13.opRevolve","SWEPT_BODY",BODY,{"disambiguationData":[OSD([sQuery(id+"F12.wireOp",EDGE,"E112"),sQuery(id+"F12.wireOp",EDGE,"E113.bottom"),sQuery(id+"F12.wireOp",EDGE,"E113.left"),sQuery(id+"F12.wireOp",EDGE,"E113.right")])]}),"instanceName":"6"});
            var Q7;
            Q7=makeQuery(id+"F14.opPattern","COPY",BODY,{"derivedFrom":makeQuery(id+"F13.opRevolve","SWEPT_BODY",BODY,{"disambiguationData":[OSD([sQuery(id+"F12.wireOp",EDGE,"E112"),sQuery(id+"F12.wireOp",EDGE,"E113.bottom"),sQuery(id+"F12.wireOp",EDGE,"E113.left"),sQuery(id+"F12.wireOp",EDGE,"E113.right")])]}),"instanceName":"7"});
            var Q8;
            Q8=makeQuery(id+"F14.opPattern","COPY",BODY,{"derivedFrom":makeQuery(id+"F13.opRevolve","SWEPT_BODY",BODY,{"disambiguationData":[OSD([sQuery(id+"F12.wireOp",EDGE,"E112"),sQuery(id+"F12.wireOp",EDGE,"E113.bottom"),sQuery(id+"F12.wireOp",EDGE,"E113.left"),sQuery(id+"F12.wireOp",EDGE,"E113.right")])]}),"instanceName":"8"});
            var Q9;
            Q9=makeQuery(id+"F14.opPattern","COPY",BODY,{"derivedFrom":makeQuery(id+"F13.opRevolve","SWEPT_BODY",BODY,{"disambiguationData":[OSD([sQuery(id+"F12.wireOp",EDGE,"E112"),sQuery(id+"F12.wireOp",EDGE,"E113.bottom"),sQuery(id+"F12.wireOp",EDGE,"E113.left"),sQuery(id+"F12.wireOp",EDGE,"E113.right")])]}),"instanceName":"9"});
            var Q10;
            Q10=makeQuery(id+"F1.opRevolve","SWEPT_BODY",BODY,{"disambiguationData":[OSD([sQuery(id+"F0.wireOp",EDGE,"E0"),sQuery(id+"F0.wireOp",EDGE,"E1"),sQuery(id+"F0.wireOp",EDGE,"E2"),sQuery(id+"F0.wireOp",EDGE,"E3"),sQuery(id+"F0.wireOp",EDGE,"E4"),sQuery(id+"F0.wireOp",EDGE,"E5"),sQuery(id+"F0.wireOp",EDGE,"E6"),sQuery(id+"F0.wireOp",EDGE,"E7"),sQuery(id+"F0.wireOp",EDGE,"E8"),sQuery(id+"F0.wireOp",EDGE,"E9"),sQuery(id+"F0.wireOp",EDGE,"E10"),sQuery(id+"F0.wireOp",EDGE,"E11"),sQuery(id+"F0.wireOp",EDGE,"E12"),sQuery(id+"F0.wireOp",EDGE,"E13"),sQuery(id+"F0.wireOp",EDGE,"E14"),sQuery(id+"F0.wireOp",EDGE,"E15"),sQuery(id+"F0.wireOp",EDGE,"E16"),sQuery(id+"F0.wireOp",EDGE,"E17"),sQuery(id+"F0.wireOp",EDGE,"E18"),sQuery(id+"F0.wireOp",EDGE,"E19"),sQuery(id+"F0.wireOp",EDGE,"E20"),sQuery(id+"F0.wireOp",EDGE,"E21"),sQuery(id+"F0.wireOp",EDGE,"E22"),sQuery(id+"F0.wireOp",EDGE,"E23"),sQuery(id+"F0.wireOp",EDGE,"E24"),sQuery(id+"F0.wireOp",EDGE,"E25"),sQuery(id+"F0.wireOp",EDGE,"E26"),sQuery(id+"F0.wireOp",EDGE,"E27"),sQuery(id+"F0.wireOp",EDGE,"E28"),sQuery(id+"F0.wireOp",EDGE,"E29"),sQuery(id+"F0.wireOp",EDGE,"E30"),sQuery(id+"F0.wireOp",EDGE,"E31"),sQuery(id+"F0.wireOp",EDGE,"E32"),sQuery(id+"F0.wireOp",EDGE,"E34"),sQuery(id+"F0.wireOp",EDGE,"E35"),sQuery(id+"F0.wireOp",EDGE,"E36"),sQuery(id+"F0.wireOp",EDGE,"E37"),sQuery(id+"F0.wireOp",EDGE,"E38")])]});
            booleanBodies(context, id + "F15", {"operationType" : BooleanOperationType.SUBTRACTION, "tools" : qUnion([Q0, Q1, Q2, Q3, Q4, Q5, Q6, Q7, Q8, Q9]), "targets" : qUnion([Q10])});
        }
        {
            var Q0;
            {var subQ0=sQuery(id+"F12.wireOp",EDGE,"E118.top");Q0=makeQuery(id+"F12.imprint","IMPRINT",FACE,{"disambiguationData":[TD([[makeQuery(id+"F12.imprint","IMPRINT",EDGE,{"derivedFrom":subQ0}),1.0]])]});}
            var Q1;
            Q1=sQuery(id+"F12.wireOp",EDGE,"E121");
            revolve(context, id + "F16", {"entities" : qUnion([Q0]), "axis" : qUnion([Q1]), "revolveType" : RevolveType.FULL});
        }
        {
            var Q0;
            Q0=makeQuery(id+"F16.opRevolve","SWEPT_BODY",BODY,{"disambiguationData":[OSD([sQuery(id+"F12.wireOp",EDGE,"E118.top"),sQuery(id+"F12.wireOp",EDGE,"E118.left"),sQuery(id+"F12.wireOp",EDGE,"E118.right"),sQuery(id+"F12.wireOp",EDGE,"E121")])]});
            var Q1;
            Q1=sQuery(id+"F0.wireOp",EDGE,"E33");
            circularPattern(context, id + "F17", {"entities" : qUnion([Q0]), "axis" : qUnion([Q1]), "angle" : 80 * degree, "instanceCount" : 5, "equalSpace" : true});
        }
        {
            var Q0;
            Q0=makeQuery(id+"F16.opRevolve","SWEPT_BODY",BODY,{"disambiguationData":[OSD([sQuery(id+"F12.wireOp",EDGE,"E118.top"),sQuery(id+"F12.wireOp",EDGE,"E118.left"),sQuery(id+"F12.wireOp",EDGE,"E118.right"),sQuery(id+"F12.wireOp",EDGE,"E121")])]});
            var Q1;
            Q1=makeQuery(id+"F17.opPattern","COPY",BODY,{"derivedFrom":makeQuery(id+"F16.opRevolve","SWEPT_BODY",BODY,{"disambiguationData":[OSD([sQuery(id+"F12.wireOp",EDGE,"E118.top"),sQuery(id+"F12.wireOp",EDGE,"E118.left"),sQuery(id+"F12.wireOp",EDGE,"E118.right"),sQuery(id+"F12.wireOp",EDGE,"E121")])]}),"instanceName":"1"});
            var Q2;
            Q2=makeQuery(id+"F17.opPattern","COPY",BODY,{"derivedFrom":makeQuery(id+"F16.opRevolve","SWEPT_BODY",BODY,{"disambiguationData":[OSD([sQuery(id+"F12.wireOp",EDGE,"E118.top"),sQuery(id+"F12.wireOp",EDGE,"E118.left"),sQuery(id+"F12.wireOp",EDGE,"E118.right"),sQuery(id+"F12.wireOp",EDGE,"E121")])]}),"instanceName":"2"});
            var Q3;
            Q3=makeQuery(id+"F17.opPattern","COPY",BODY,{"derivedFrom":makeQuery(id+"F16.opRevolve","SWEPT_BODY",BODY,{"disambiguationData":[OSD([sQuery(id+"F12.wireOp",EDGE,"E118.top"),sQuery(id+"F12.wireOp",EDGE,"E118.left"),sQuery(id+"F12.wireOp",EDGE,"E118.right"),sQuery(id+"F12.wireOp",EDGE,"E121")])]}),"instanceName":"3"});
            var Q4;
            Q4=makeQuery(id+"F17.opPattern","COPY",BODY,{"derivedFrom":makeQuery(id+"F16.opRevolve","SWEPT_BODY",BODY,{"disambiguationData":[OSD([sQuery(id+"F12.wireOp",EDGE,"E118.top"),sQuery(id+"F12.wireOp",EDGE,"E118.left"),sQuery(id+"F12.wireOp",EDGE,"E118.right"),sQuery(id+"F12.wireOp",EDGE,"E121")])]}),"instanceName":"4"});
            var Q5;
            Q5=makeQuery(id+"F1.opRevolve","SWEPT_BODY",BODY,{"disambiguationData":[OSD([sQuery(id+"F0.wireOp",EDGE,"E0"),sQuery(id+"F0.wireOp",EDGE,"E1"),sQuery(id+"F0.wireOp",EDGE,"E2"),sQuery(id+"F0.wireOp",EDGE,"E3"),sQuery(id+"F0.wireOp",EDGE,"E4"),sQuery(id+"F0.wireOp",EDGE,"E5"),sQuery(id+"F0.wireOp",EDGE,"E6"),sQuery(id+"F0.wireOp",EDGE,"E7"),sQuery(id+"F0.wireOp",EDGE,"E8"),sQuery(id+"F0.wireOp",EDGE,"E9"),sQuery(id+"F0.wireOp",EDGE,"E10"),sQuery(id+"F0.wireOp",EDGE,"E11"),sQuery(id+"F0.wireOp",EDGE,"E12"),sQuery(id+"F0.wireOp",EDGE,"E13"),sQuery(id+"F0.wireOp",EDGE,"E14"),sQuery(id+"F0.wireOp",EDGE,"E15"),sQuery(id+"F0.wireOp",EDGE,"E16"),sQuery(id+"F0.wireOp",EDGE,"E17"),sQuery(id+"F0.wireOp",EDGE,"E18"),sQuery(id+"F0.wireOp",EDGE,"E19"),sQuery(id+"F0.wireOp",EDGE,"E20"),sQuery(id+"F0.wireOp",EDGE,"E21"),sQuery(id+"F0.wireOp",EDGE,"E22"),sQuery(id+"F0.wireOp",EDGE,"E23"),sQuery(id+"F0.wireOp",EDGE,"E24"),sQuery(id+"F0.wireOp",EDGE,"E25"),sQuery(id+"F0.wireOp",EDGE,"E26"),sQuery(id+"F0.wireOp",EDGE,"E27"),sQuery(id+"F0.wireOp",EDGE,"E28"),sQuery(id+"F0.wireOp",EDGE,"E29"),sQuery(id+"F0.wireOp",EDGE,"E30"),sQuery(id+"F0.wireOp",EDGE,"E31"),sQuery(id+"F0.wireOp",EDGE,"E32"),sQuery(id+"F0.wireOp",EDGE,"E34"),sQuery(id+"F0.wireOp",EDGE,"E35"),sQuery(id+"F0.wireOp",EDGE,"E36"),sQuery(id+"F0.wireOp",EDGE,"E37"),sQuery(id+"F0.wireOp",EDGE,"E38")])]});
            booleanBodies(context, id + "F18", {"operationType" : BooleanOperationType.SUBTRACTION, "tools" : qUnion([Q0, Q1, Q2, Q3, Q4]), "targets" : qUnion([Q5])});
        }
        {
            var Q0;
            Q0=makeQuery(id+"F1.opRevolve","SWEPT_FACE",FACE,{"disambiguationData":[OSD([sQuery(id+"F0.wireOp",EDGE,"E30")])]});
            cPlane(context, id + "F19", {"entities" : qUnion([Q0]), "cplaneType" : CPlaneType.OFFSET, "offset" : 0.1 * mm, "width" : 150 * mm, "height" : 150 * mm});
        }
        {
            var Q0;
            Q0=qCreatedBy(id+"F19.planeOp",FACE);
            var sketch = newSketch(context, id + "F20", { "sketchPlane" : qUnion([Q0])});
            skCircle(sketch, "E122", {"center": v(-2, 63) * mm, "radius": 50 * mm});
            skCircle(sketch, "E123", {"center": v(60.19, 18.2) * mm, "radius": 50 * mm});
            skLineSegment(sketch, "E124", {"start": v(0, 0) * mm, "end": v(60.7, 16.27) * mm, "construction": true});
            skLineSegment(sketch, "E125", {"start": v(0, 2.07) * mm, "end": v(60.19, 18.2) * mm, "construction": true});
            skPoint(sketch, "E126", {"position": v(11.89, 5.26) * mm});
            skLineSegment(sketch, "E127", {"start": v(60.19, 18.2) * mm, "end": v(60.7, 16.27) * mm, "construction": true});
            skSolve(sketch);
        }
        {
            var Q0;
            Q0 = qSketchRegion(id + "F20", true);
            extrude(context, id + "F21", {"entities" : qUnion([Q0]), "depth" : 5 * mm});
        }
        {
            var Q0;
            Q0=makeQuery(id+"F21.opExtrude","SWEPT_BODY",BODY,{"disambiguationData":[OSD([sQuery(id+"F20.wireOp",EDGE,"E122"),sQuery(id+"F20.wireOp",EDGE,"E123")])]});
            var Q1;
            Q1=makeQuery(id+"F1.opRevolve","SWEPT_BODY",BODY,{"disambiguationData":[OSD([sQuery(id+"F0.wireOp",EDGE,"E0"),sQuery(id+"F0.wireOp",EDGE,"E1"),sQuery(id+"F0.wireOp",EDGE,"E2"),sQuery(id+"F0.wireOp",EDGE,"E3"),sQuery(id+"F0.wireOp",EDGE,"E4"),sQuery(id+"F0.wireOp",EDGE,"E5"),sQuery(id+"F0.wireOp",EDGE,"E6"),sQuery(id+"F0.wireOp",EDGE,"E7"),sQuery(id+"F0.wireOp",EDGE,"E8"),sQuery(id+"F0.wireOp",EDGE,"E9"),sQuery(id+"F0.wireOp",EDGE,"E10"),sQuery(id+"F0.wireOp",EDGE,"E11"),sQuery(id+"F0.wireOp",EDGE,"E12"),sQuery(id+"F0.wireOp",EDGE,"E13"),sQuery(id+"F0.wireOp",EDGE,"E14"),sQuery(id+"F0.wireOp",EDGE,"E15"),sQuery(id+"F0.wireOp",EDGE,"E16"),sQuery(id+"F0.wireOp",EDGE,"E17"),sQuery(id+"F0.wireOp",EDGE,"E18"),sQuery(id+"F0.wireOp",EDGE,"E19"),sQuery(id+"F0.wireOp",EDGE,"E20"),sQuery(id+"F0.wireOp",EDGE,"E21"),sQuery(id+"F0.wireOp",EDGE,"E22"),sQuery(id+"F0.wireOp",EDGE,"E23"),sQuery(id+"F0.wireOp",EDGE,"E24"),sQuery(id+"F0.wireOp",EDGE,"E25"),sQuery(id+"F0.wireOp",EDGE,"E26"),sQuery(id+"F0.wireOp",EDGE,"E27"),sQuery(id+"F0.wireOp",EDGE,"E28"),sQuery(id+"F0.wireOp",EDGE,"E29"),sQuery(id+"F0.wireOp",EDGE,"E30"),sQuery(id+"F0.wireOp",EDGE,"E31"),sQuery(id+"F0.wireOp",EDGE,"E32"),sQuery(id+"F0.wireOp",EDGE,"E34"),sQuery(id+"F0.wireOp",EDGE,"E35"),sQuery(id+"F0.wireOp",EDGE,"E36"),sQuery(id+"F0.wireOp",EDGE,"E37"),sQuery(id+"F0.wireOp",EDGE,"E38")])]});
            booleanBodies(context, id + "F22", {"operationType" : BooleanOperationType.SUBTRACTION, "tools" : qUnion([Q0]), "targets" : qUnion([Q1])});
        }
        {
            var Q0;
            Q0=makeQuery(id+"F1.opRevolve","SWEPT_FACE",FACE,{"disambiguationData":[OSD([sQuery(id+"F0.wireOp",EDGE,"E30")])]});
            var sketch = newSketch(context, id + "F23", { "sketchPlane" : qUnion([Q0])});
            skCircle(sketch, "E128", {"center": v(0, 0) * mm, "radius": 19 * mm, "construction": true});
            skLineSegment(sketch, "E129", {"start": v(17.62, 7.12) * mm, "end": v(0, 0) * mm, "construction": true});
            skLineSegment(sketch, "E130", {"start": v(5.87, 18.07) * mm, "end": v(0, 0) * mm, "construction": true});
            skLineSegment(sketch, "E131", {"start": v(-12.71, 14.12) * mm, "end": v(0, 0) * mm, "construction": true});
            skLineSegment(sketch, "E132", {"start": v(-17.62, -7.12) * mm, "end": v(0, 0) * mm, "construction": true});
            skLineSegment(sketch, "E133", {"start": v(-14.55, -12.21) * mm, "end": v(0, 0) * mm, "construction": true});
            skLineSegment(sketch, "E134", {"start": v(-9.5, -16.45) * mm, "end": v(0, 0) * mm, "construction": true});
            skLineSegment(sketch, "E135", {"start": v(-3.3, -18.71) * mm, "end": v(0, 0) * mm, "construction": true});
            skLineSegment(sketch, "E136", {"start": v(3.3, -18.71) * mm, "end": v(0, 0) * mm, "construction": true});
            skLineSegment(sketch, "E137", {"start": v(9.5, -16.45) * mm, "end": v(0, 0) * mm, "construction": true});
            skLineSegment(sketch, "E138", {"start": v(14.55, -12.21) * mm, "end": v(0, 0) * mm, "construction": true});
            skLineSegment(sketch, "E139", {"start": v(17.85, -6.5) * mm, "end": v(0, 0) * mm, "construction": true});
            skLineSegment(sketch, "E140", {"start": v(19, 0) * mm, "end": v(0, 0) * mm, "construction": true});
            skSolve(sketch);
        }
        {
            var Q0;
            Q0=sQuery(id+"F23.wireOp",VERTEX,"E133.start");
            var Q1;
            Q1=sQuery(id+"F23.wireOp",VERTEX,"E134.start");
            var Q2;
            Q2=sQuery(id+"F23.wireOp",VERTEX,"E135.start");
            var Q3;
            Q3=sQuery(id+"F23.wireOp",VERTEX,"E136.start");
            var Q4;
            Q4=sQuery(id+"F23.wireOp",VERTEX,"E137.start");
            var Q5;
            Q5=sQuery(id+"F23.wireOp",VERTEX,"E138.start");
            var Q6;
            Q6=sQuery(id+"F23.wireOp",VERTEX,"E139.start");
            var Q7;
            Q7=sQuery(id+"F23.wireOp",VERTEX,"E140.start");
            var Q8;
            Q8=makeQuery(id+"F1.opRevolve","SWEPT_BODY",BODY,{"disambiguationData":[OSD([sQuery(id+"F0.wireOp",EDGE,"E0"),sQuery(id+"F0.wireOp",EDGE,"E1"),sQuery(id+"F0.wireOp",EDGE,"E2"),sQuery(id+"F0.wireOp",EDGE,"E3"),sQuery(id+"F0.wireOp",EDGE,"E4"),sQuery(id+"F0.wireOp",EDGE,"E5"),sQuery(id+"F0.wireOp",EDGE,"E6"),sQuery(id+"F0.wireOp",EDGE,"E7"),sQuery(id+"F0.wireOp",EDGE,"E8"),sQuery(id+"F0.wireOp",EDGE,"E9"),sQuery(id+"F0.wireOp",EDGE,"E10"),sQuery(id+"F0.wireOp",EDGE,"E11"),sQuery(id+"F0.wireOp",EDGE,"E12"),sQuery(id+"F0.wireOp",EDGE,"E13"),sQuery(id+"F0.wireOp",EDGE,"E14"),sQuery(id+"F0.wireOp",EDGE,"E15"),sQuery(id+"F0.wireOp",EDGE,"E16"),sQuery(id+"F0.wireOp",EDGE,"E17"),sQuery(id+"F0.wireOp",EDGE,"E18"),sQuery(id+"F0.wireOp",EDGE,"E19"),sQuery(id+"F0.wireOp",EDGE,"E20"),sQuery(id+"F0.wireOp",EDGE,"E21"),sQuery(id+"F0.wireOp",EDGE,"E22"),sQuery(id+"F0.wireOp",EDGE,"E23"),sQuery(id+"F0.wireOp",EDGE,"E24"),sQuery(id+"F0.wireOp",EDGE,"E25"),sQuery(id+"F0.wireOp",EDGE,"E26"),sQuery(id+"F0.wireOp",EDGE,"E27"),sQuery(id+"F0.wireOp",EDGE,"E28"),sQuery(id+"F0.wireOp",EDGE,"E29"),sQuery(id+"F0.wireOp",EDGE,"E30"),sQuery(id+"F0.wireOp",EDGE,"E31"),sQuery(id+"F0.wireOp",EDGE,"E32"),sQuery(id+"F0.wireOp",EDGE,"E34"),sQuery(id+"F0.wireOp",EDGE,"E35"),sQuery(id+"F0.wireOp",EDGE,"E36"),sQuery(id+"F0.wireOp",EDGE,"E37"),sQuery(id+"F0.wireOp",EDGE,"E38")])]});
            hole(context, id + "F24", {"style" : HoleStyle.SIMPLE, "endStyle" : HoleEndStyle.THROUGH, "holeDiameter" : 1 * mm, "tappedDepth" : 12 * mm, "tapClearance" : 3, "locations" : qUnion([Q0, Q1, Q2, Q3, Q4, Q5, Q6, Q7]), "scope" : qUnion([Q8])});
        }
        {
            var Q0;
            Q0=sQuery(id+"F23.wireOp",VERTEX,"E129.start");
            var Q1;
            Q1=sQuery(id+"F23.wireOp",VERTEX,"E130.start");
            var Q2;
            Q2=sQuery(id+"F23.wireOp",VERTEX,"E131.start");
            var Q3;
            Q3=sQuery(id+"F23.wireOp",VERTEX,"E132.start");
            var Q4;
            Q4=makeQuery(id+"F1.opRevolve","SWEPT_BODY",BODY,{"disambiguationData":[OSD([sQuery(id+"F0.wireOp",EDGE,"E0"),sQuery(id+"F0.wireOp",EDGE,"E1"),sQuery(id+"F0.wireOp",EDGE,"E2"),sQuery(id+"F0.wireOp",EDGE,"E3"),sQuery(id+"F0.wireOp",EDGE,"E4"),sQuery(id+"F0.wireOp",EDGE,"E5"),sQuery(id+"F0.wireOp",EDGE,"E6"),sQuery(id+"F0.wireOp",EDGE,"E7"),sQuery(id+"F0.wireOp",EDGE,"E8"),sQuery(id+"F0.wireOp",EDGE,"E9"),sQuery(id+"F0.wireOp",EDGE,"E10"),sQuery(id+"F0.wireOp",EDGE,"E11"),sQuery(id+"F0.wireOp",EDGE,"E12"),sQuery(id+"F0.wireOp",EDGE,"E13"),sQuery(id+"F0.wireOp",EDGE,"E14"),sQuery(id+"F0.wireOp",EDGE,"E15"),sQuery(id+"F0.wireOp",EDGE,"E16"),sQuery(id+"F0.wireOp",EDGE,"E17"),sQuery(id+"F0.wireOp",EDGE,"E18"),sQuery(id+"F0.wireOp",EDGE,"E19"),sQuery(id+"F0.wireOp",EDGE,"E20"),sQuery(id+"F0.wireOp",EDGE,"E21"),sQuery(id+"F0.wireOp",EDGE,"E22"),sQuery(id+"F0.wireOp",EDGE,"E23"),sQuery(id+"F0.wireOp",EDGE,"E24"),sQuery(id+"F0.wireOp",EDGE,"E25"),sQuery(id+"F0.wireOp",EDGE,"E26"),sQuery(id+"F0.wireOp",EDGE,"E27"),sQuery(id+"F0.wireOp",EDGE,"E28"),sQuery(id+"F0.wireOp",EDGE,"E29"),sQuery(id+"F0.wireOp",EDGE,"E30"),sQuery(id+"F0.wireOp",EDGE,"E31"),sQuery(id+"F0.wireOp",EDGE,"E32"),sQuery(id+"F0.wireOp",EDGE,"E34"),sQuery(id+"F0.wireOp",EDGE,"E35"),sQuery(id+"F0.wireOp",EDGE,"E36"),sQuery(id+"F0.wireOp",EDGE,"E37"),sQuery(id+"F0.wireOp",EDGE,"E38")])]});
            hole(context, id + "F25", {"style" : HoleStyle.SIMPLE, "endStyle" : HoleEndStyle.THROUGH, "holeDiameter" : 2 * mm, "tappedDepth" : 12 * mm, "tapClearance" : 3, "locations" : qUnion([Q0, Q1, Q2, Q3]), "scope" : qUnion([Q4])});
        }
    });
